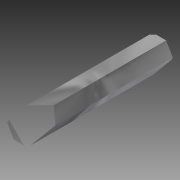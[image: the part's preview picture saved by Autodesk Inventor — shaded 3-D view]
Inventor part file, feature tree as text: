
AUTODESK INVENTOR PART (.ipt)
format: ipt  version: 2014 (Build 180170000, 170)  size: 94,208 bytes
history: native  units: in
note: dims shown in document units (in); Inventor stores cm internally (conversion verified against a paired STEP export)
features: extrude x1, sketch x1
ambient origin geometry x8: Origin, YZ Plane, XZ Plane, XY Plane, X Axis, Y Axis, Z Axis, Center Point
bodies: Solid1 (feature_tree)
feature tree (2):
  extrude  "Extrusion1"  Depth=3.0in TaperAngle=0.0deg
  sketch  "Sketch1"  dims[d0=0.5in d1=3.0in d2=0.0in]
